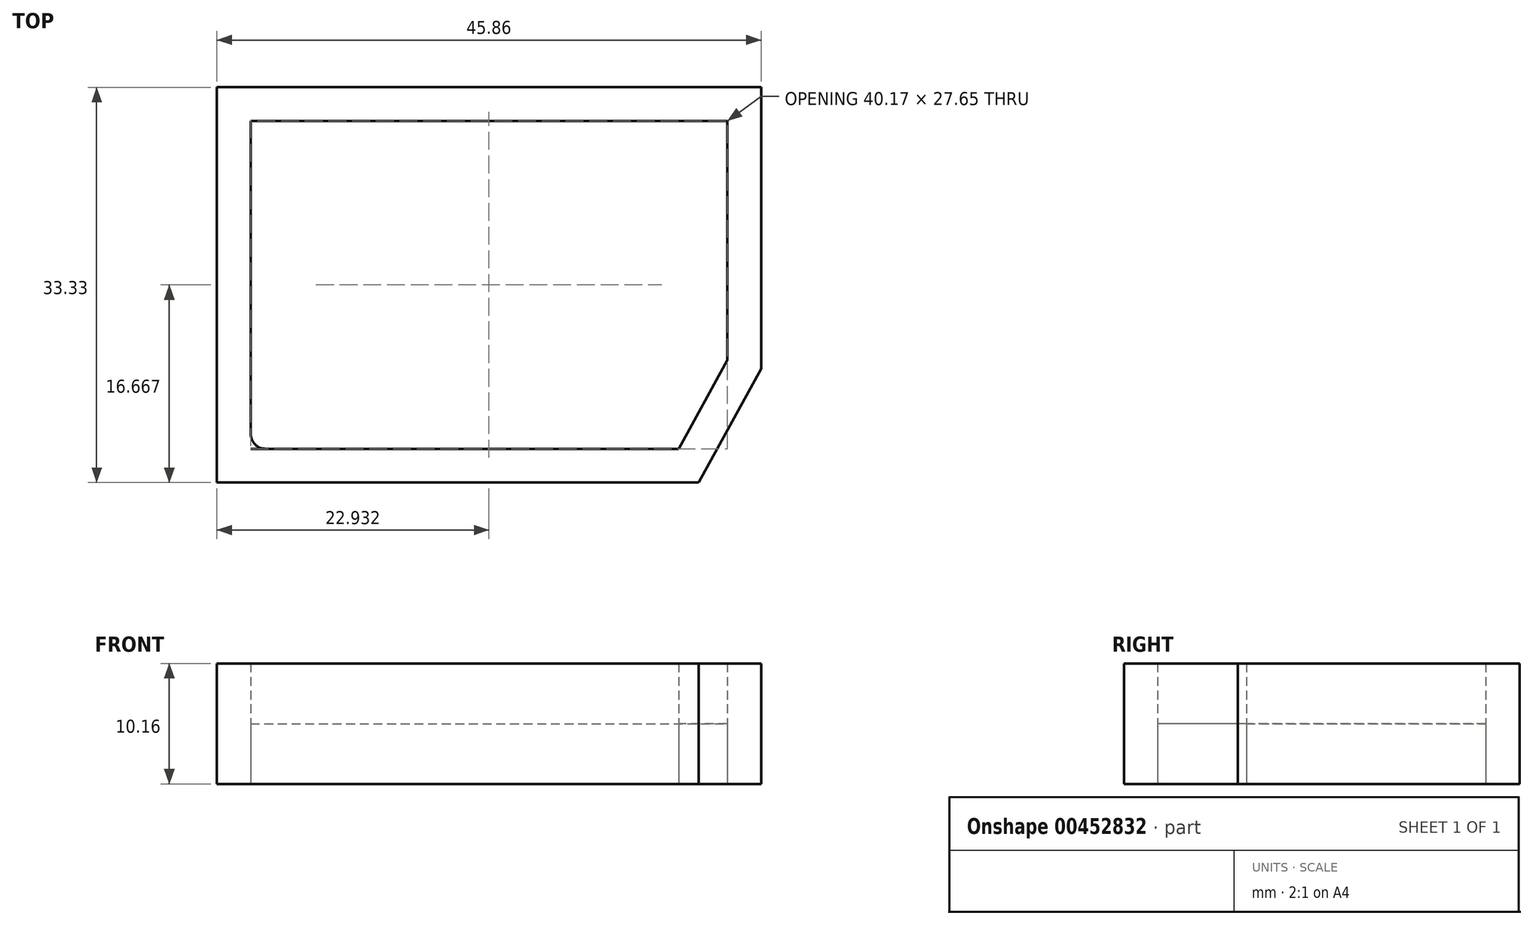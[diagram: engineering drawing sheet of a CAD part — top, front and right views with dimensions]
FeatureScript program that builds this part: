
annotation { "Feature Type Name" : "Feature", "Feature Type Description" : "" }
export const myFeature = defineFeature(function(context is Context, id is Id, definition is map)
    precondition{}
    {
        {
            var Q0;
            Q0=qCreatedBy(makeId("Top.planeOp"),FACE);
            var sketch = newSketch(context, id + "F0", { "sketchPlane" : qUnion([Q0])});
            skLineSegment(sketch, "E0.bottom", {"start": v(-47.05, 2.4) * mm, "end": v(-6.88, 2.4) * mm});
            skLineSegment(sketch, "E0.left", {"start": v(-47.05, 2.4) * mm, "end": v(-47.05, -25.25) * mm});
            skLineSegment(sketch, "E1", {"start": v(-6.88, -17.77) * mm, "end": v(-11, -25.25) * mm});
            skLineSegment(sketch, "E2", {"start": v(-47.05, -25.25) * mm, "end": v(-11, -25.25) * mm});
            skLineSegment(sketch, "E3", {"start": v(-6.88, -17.77) * mm, "end": v(-6.88, 2.4) * mm});
            skLineSegment(sketch, "E4.0", {"start": v(-4.04, -18.5) * mm, "end": v(-9.31, -28.1) * mm});
            skLineSegment(sketch, "E4.1", {"start": v(-49.9, -28.1) * mm, "end": v(-9.31, -28.1) * mm});
            skLineSegment(sketch, "E4.2", {"start": v(-4.04, -18.5) * mm, "end": v(-4.04, 5.24) * mm});
            skLineSegment(sketch, "E4.3", {"start": v(-49.9, 5.24) * mm, "end": v(-4.04, 5.24) * mm});
            skLineSegment(sketch, "E4.4", {"start": v(-49.9, 5.24) * mm, "end": v(-49.9, -28.1) * mm});
            skSolve(sketch);
        }
        {
            var Q0;
            Q0=makeQuery(id+"F0.imprint","IMPRINT",FACE,{"disambiguationData":[TD([[makeQuery(id+"F0.imprint","IMPRINT",EDGE,{"derivedFrom":sQuery(id+"F0.wireOp",EDGE,"E0.bottom")}),1.0]])]});
            extrude(context, id + "F1", {"entities" : qUnion([Q0]), "depth" : 10.16 * mm});
        }
        {
            var Q0;
            Q0=makeQuery(id+"F0.imprint","IMPRINT",FACE,{"disambiguationData":[TD([[makeQuery(id+"F0.imprint","IMPRINT",EDGE,{"derivedFrom":sQuery(id+"F0.wireOp",EDGE,"E0.bottom")}),-1.0]])]});
            var sketch = newSketch(context, id + "F2", { "sketchPlane" : qUnion([Q0])});
            skSolve(sketch);
        }
        {
            var Q0;
            Q0 = qSketchRegion(id + "F2", true);
            var Q1;
            Q1=makeQuery(id+"F2.imprint","IMPRINT",FACE,{"disambiguationData":[TD([[makeQuery(id+"F2.imprint","IMPRINT",EDGE,{"derivedFrom":makeQuery(id+"F0.imprint","IMPRINT",EDGE,{"derivedFrom":sQuery(id+"F0.wireOp",EDGE,"E0.bottom")})}),-1.0]])]});
            extrude(context, id + "F3", {"entities" : qUnion([Q0, Q1]), "depth" : 5.08 * mm});
        }
        {
            var Q0;
            Q0=makeQuery(id+"F1.opExtrude","SWEPT_EDGE",EDGE,{"disambiguationData":[OSD([sQuery(id+"F0.wireOp",EDGE,"E0.left"),sQuery(id+"F0.wireOp",EDGE,"E2")])]});
            fillet(context, id + "F4", {"entities" : qUnion([Q0]), "radius" : 1.27 * mm, "tangentPropagation" : true, "allowEdgeOverflow" : false});
        }
    });
